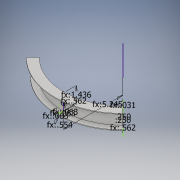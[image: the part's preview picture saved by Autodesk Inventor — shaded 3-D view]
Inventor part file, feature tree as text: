
AUTODESK INVENTOR PART (.ipt)
format: ipt  version: 2017 (Build 210142000, 142)  size: 171,520 bytes
history: native  units: in
note: dims shown in document units (in); Inventor stores cm internally (conversion verified against a paired STEP export)
features: sketch x5, extrude x4, revolve x1, plane x1
ambient origin geometry x8: Origin, YZ Plane, XZ Plane, XY Plane, X Axis, Y Axis, Z Axis, Center Point
bodies: Solid1 (feature_tree)
feature tree (11):
  revolve  "Revolution1"  [1 undecoded]
  plane  "Work Plane1"
  sketch  "Sketch2"  dims[d3=1.4364in d4=0.0625in]
  extrude  "Extrusion2"  Depth=0.0625in
  extrude  "Extrusion3"  TaperAngle=90.0deg  [1 undecoded]
  extrude  "Extrusion4"  Depth=0.375in
  extrude  "Extrusion5"  Depth=0.0312in TaperAngle=0.0deg
  sketch  "Sketch5"  dims[d11=0.3125in d12=1.0in d13=0.0in d14=0.0156in d15=0.0in d16=0.25in d17=0.0625in d18=0.0in d19=135.0deg d20=0.0in d21=0.0in d23=0.0312in d24=0.25in d25=0.25in d27=0.562in]
  sketch  "Sketch1"  dims[d1=0.5536in d2=0.0625in]
  sketch  "Sketch3"  dims[d5=0.0625in d6=90.0deg]
  sketch  "Sketch4"  dims[d7=0.562in d8=0.375in]
note: 2 required parameter values undecoded (feature->parameter linkage not recoverable at this tier; creation-order binding heuristic only, values carry confidence <= 0.55)